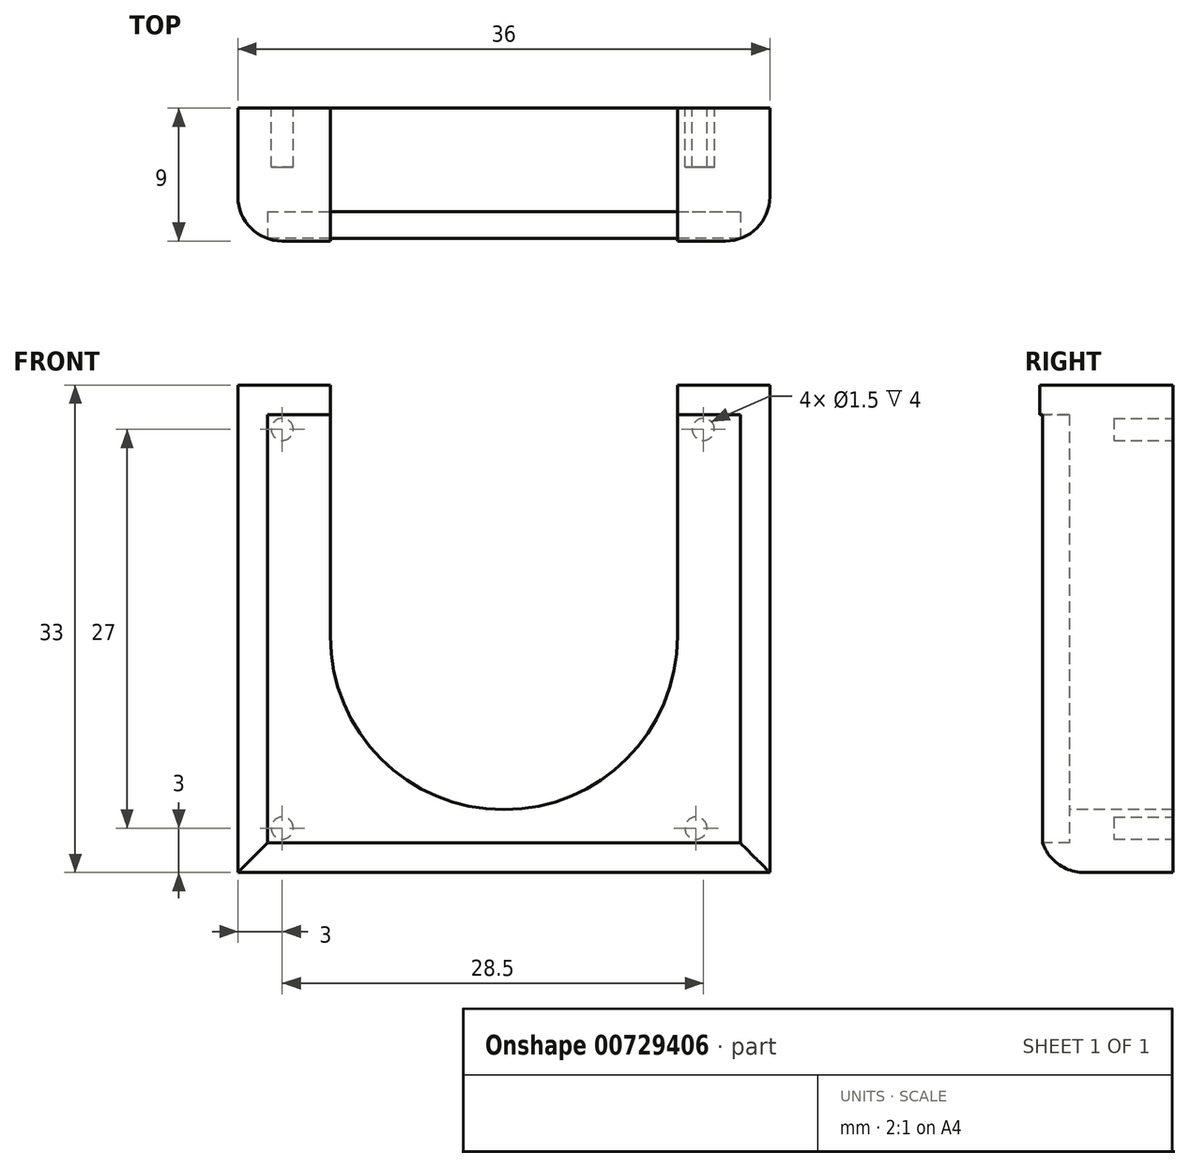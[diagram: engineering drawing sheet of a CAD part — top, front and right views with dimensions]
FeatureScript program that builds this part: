
annotation { "Feature Type Name" : "Feature", "Feature Type Description" : "" }
export const myFeature = defineFeature(function(context is Context, id is Id, definition is map)
    precondition{}
    {
        {
            var Q0;
            Q0=qCreatedBy(makeId("Front.planeOp"),FACE);
            var sketch = newSketch(context, id + "F0", { "sketchPlane" : qUnion([Q0])});
            skLineSegment(sketch, "E0.bottom", {"start": v(0, 0) * mm, "end": v(36, 0) * mm});
            skLineSegment(sketch, "E0.top", {"start": v(0, 33) * mm, "end": v(36, 33) * mm});
            skLineSegment(sketch, "E0.left", {"start": v(0, 0) * mm, "end": v(0, 33) * mm});
            skLineSegment(sketch, "E0.right", {"start": v(36, 0) * mm, "end": v(36, 33) * mm});
            skSolve(sketch);
        }
        {
            var Q0;
            Q0 = qSketchRegion(id + "F0", true);
            extrude(context, id + "F1", {"entities" : qUnion([Q0]), "depth" : 9 * mm, "offsetDistance" : 25 * mm});
        }
        {
            var Q0;
            Q0=makeQuery(id+"F1.opExtrude","CAP_FACE",FACE,{"disambiguationData":[OSD([sQuery(id+"F0.wireOp",EDGE,"E0.bottom"),sQuery(id+"F0.wireOp",EDGE,"E0.top"),sQuery(id+"F0.wireOp",EDGE,"E0.left"),sQuery(id+"F0.wireOp",EDGE,"E0.right")])],"isStart":false});
            var sketch = newSketch(context, id + "F2", { "sketchPlane" : qUnion([Q0])});
            skCircle(sketch, "E1", {"center": v(18, 16) * mm, "radius": 11.75 * mm});
            skPoint(sketch, "E1.centerSnap0", {"position": v(36, 16) * mm});
            skPoint(sketch, "E1.centerSnap1", {"position": v(18, 33) * mm});
            skLineSegment(sketch, "E2", {"start": v(6.25, 16) * mm, "end": v(6.25, 33) * mm});
            skLineSegment(sketch, "E3", {"start": v(29.75, 16) * mm, "end": v(29.75, 33) * mm});
            skLineSegment(sketch, "E4", {"start": v(29.75, 33) * mm, "end": v(6.25, 33) * mm});
            skSolve(sketch);
        }
        {
            var Q0;
            Q0 = qSketchRegion(id + "F2", true);
            extrude(context, id + "F3", {"entities" : qUnion([Q0]), "operationType" : NewBodyOperationType.REMOVE, "oppositeDirection" : true, "depth" : 25 * mm, "offsetDistance" : 25 * mm});
        }
        {
            var Q0;
            Q0=makeQuery(id+"F1.opExtrude","CAP_FACE",FACE,{"disambiguationData":[OSD([sQuery(id+"F0.wireOp",EDGE,"E0.bottom"),sQuery(id+"F0.wireOp",EDGE,"E0.top"),sQuery(id+"F0.wireOp",EDGE,"E0.left"),sQuery(id+"F0.wireOp",EDGE,"E0.right")])],"isStart":false});
            var sketch = newSketch(context, id + "F4", { "sketchPlane" : qUnion([Q0])});
            skLineSegment(sketch, "E5.bottom", {"start": v(2, 31) * mm, "end": v(34, 31) * mm});
            skLineSegment(sketch, "E5.top", {"start": v(2, 2) * mm, "end": v(34, 2) * mm});
            skLineSegment(sketch, "E5.left", {"start": v(2, 31) * mm, "end": v(2, 2) * mm});
            skLineSegment(sketch, "E5.right", {"start": v(34, 31) * mm, "end": v(34, 2) * mm});
            skSolve(sketch);
        }
        {
            var Q0;
            Q0 = qSketchRegion(id + "F4", true);
            extrude(context, id + "F5", {"entities" : qUnion([Q0]), "operationType" : NewBodyOperationType.REMOVE, "oppositeDirection" : true, "depth" : 2 * mm, "offsetDistance" : 25 * mm});
        }
        {
            var Q0;
            Q0=makeQuery(id+"F1.opExtrude","CAP_FACE",FACE,{"disambiguationData":[OSD([sQuery(id+"F0.wireOp",EDGE,"E0.bottom"),sQuery(id+"F0.wireOp",EDGE,"E0.top"),sQuery(id+"F0.wireOp",EDGE,"E0.left"),sQuery(id+"F0.wireOp",EDGE,"E0.right")])],"isStart":true});
            var sketch = newSketch(context, id + "F6", { "sketchPlane" : qUnion([Q0])});
            skCircle(sketch, "E6", {"center": v(-31.5, 30) * mm, "radius": 0.75 * mm});
            skCircle(sketch, "E7", {"center": v(-3, 30) * mm, "radius": 0.75 * mm});
            skCircle(sketch, "E8", {"center": v(-3, 3) * mm, "radius": 0.75 * mm});
            skCircle(sketch, "E9", {"center": v(-31, 3) * mm, "radius": 0.75 * mm});
            skSolve(sketch);
        }
        {
            var Q0;
            Q0 = qSketchRegion(id + "F6", true);
            extrude(context, id + "F7", {"entities" : qUnion([Q0]), "operationType" : NewBodyOperationType.REMOVE, "oppositeDirection" : true, "depth" : 4 * mm, "offsetDistance" : 25 * mm});
        }
        {
            var Q0;
            Q0=makeQuery(id+"F1.opExtrude","CAP_EDGE",EDGE,{"disambiguationData":[OSD([sQuery(id+"F0.wireOp",EDGE,"E0.right")])],"isStart":false});
            var Q1;
            Q1=makeQuery(id+"F1.opExtrude","CAP_EDGE",EDGE,{"disambiguationData":[OSD([sQuery(id+"F0.wireOp",EDGE,"E0.bottom")])],"isStart":false});
            var Q2;
            Q2=makeQuery(id+"F1.opExtrude","CAP_EDGE",EDGE,{"disambiguationData":[OSD([sQuery(id+"F0.wireOp",EDGE,"E0.left")])],"isStart":false});
            fillet(context, id + "F8", {"entities" : qUnion([Q0, Q1, Q2]), "radius" : 3 * mm, "tangentPropagation" : true, "allowEdgeOverflow" : false});
        }
    });
